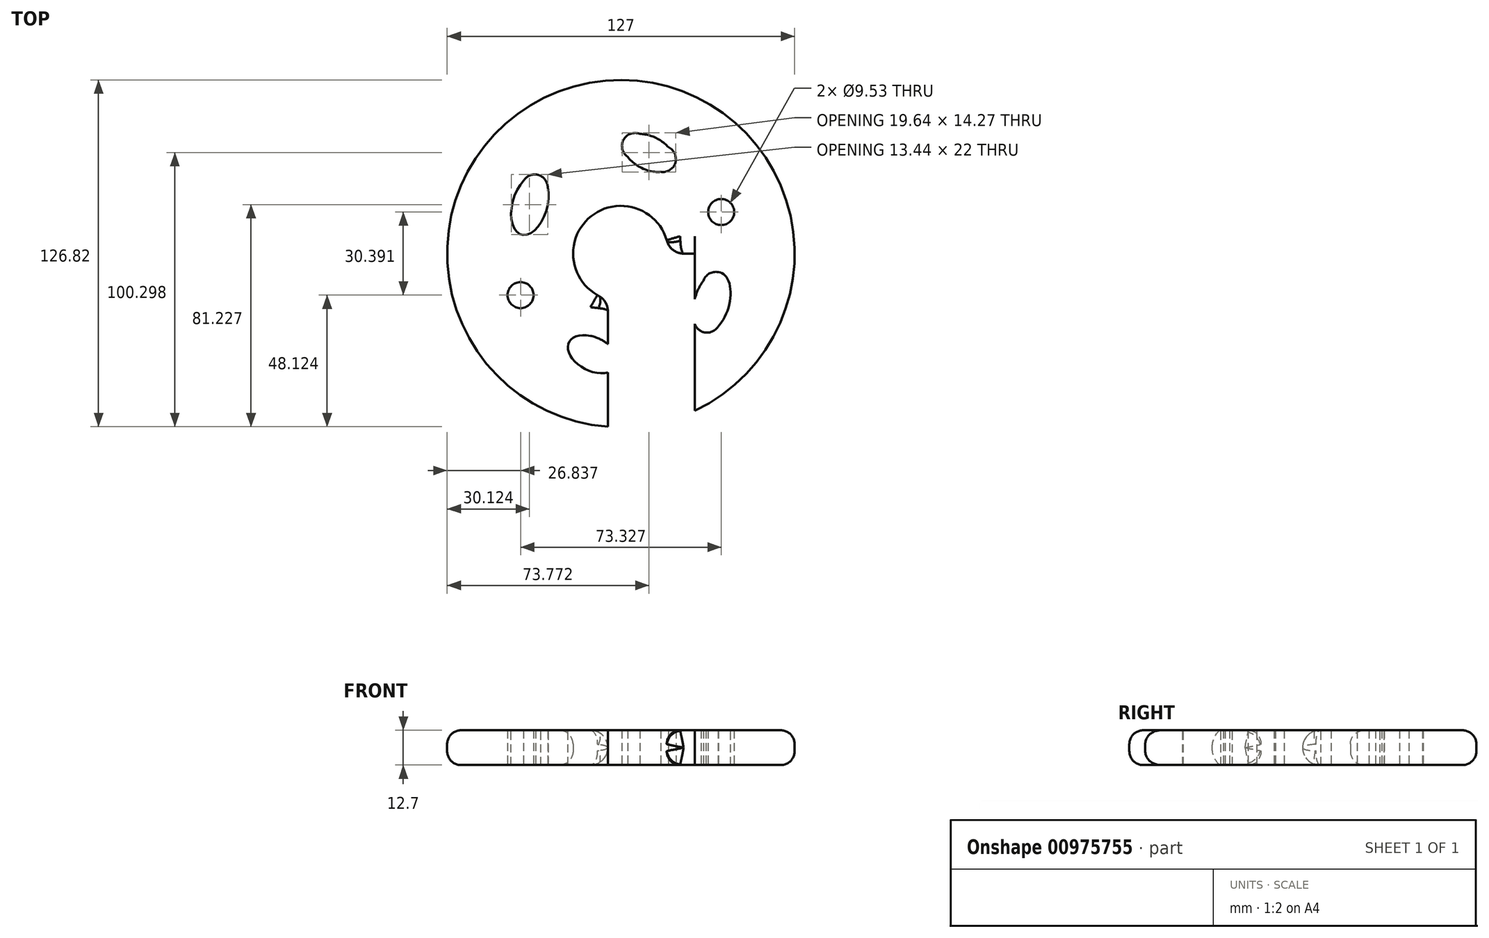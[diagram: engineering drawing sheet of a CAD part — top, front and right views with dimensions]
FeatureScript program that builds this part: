
annotation { "Feature Type Name" : "Feature", "Feature Type Description" : "" }
export const myFeature = defineFeature(function(context is Context, id is Id, definition is map)
    precondition{}
    {
        {
            var Q0;
            Q0=qCreatedBy(makeId("Top.planeOp"),FACE);
            var sketch = newSketch(context, id + "F0", { "sketchPlane" : qUnion([Q0])});
            skCircle(sketch, "E0", {"center": v(0, 0) * mm, "radius": 63.5 * mm});
            skCircle(sketch, "E1", {"center": v(0, 0) * mm, "radius": 17.46 * mm});
            skCircle(sketch, "E2", {"center": v(31.5, -24.15) * mm, "radius": 4.76 * mm});
            skCircle(sketch, "E3.1.0", {"center": v(36.66, 15.2) * mm, "radius": 4.76 * mm});
            skCircle(sketch, "E3.2.0", {"center": v(5.17, 39.35) * mm, "radius": 4.76 * mm});
            skCircle(sketch, "E3.3.0", {"center": v(-31.5, 24.15) * mm, "radius": 4.76 * mm});
            skCircle(sketch, "E3.4.0", {"center": v(-36.66, -15.2) * mm, "radius": 4.76 * mm});
            skCircle(sketch, "E3.5.0", {"center": v(-5.17, -39.35) * mm, "radius": 4.76 * mm});
            skCircle(sketch, "E4", {"center": v(34.67, -11.45) * mm, "radius": 4.76 * mm});
            skCircle(sketch, "E5", {"center": v(-13.19, -29.5) * mm, "radius": 4.76 * mm});
            skCircle(sketch, "E6", {"center": v(-40.13, 9.65) * mm, "radius": 4.76 * mm});
            skCircle(sketch, "E7", {"center": v(15.34, 34.59) * mm, "radius": 4.76 * mm});
            skEllipse(sketch, "E8", {"center": v(33.25, -17.84) * mm, "majorRadius": 11.35 * mm, "minorRadius": 6.37 * mm, "majorAxis": v(0.27, 0.96)});
            skEllipse(sketch, "E9.1.0", {"center": v(-33.25, 17.84) * mm, "majorRadius": 11.35 * mm, "minorRadius": 6.37 * mm, "majorAxis": v(-0.27, -0.96)});
            skEllipse(sketch, "E10", {"center": v(10.2, 36.8) * mm, "majorRadius": 9.78 * mm, "minorRadius": 6.1 * mm, "majorAxis": v(-0.9, 0.44)});
            skEllipse(sketch, "E11.1.0", {"center": v(-10.2, -36.8) * mm, "majorRadius": 9.78 * mm, "minorRadius": 6.1 * mm, "majorAxis": v(0.9, -0.44)});
            skSolve(sketch);
        }
        {
            var Q0;
            Q0=makeQuery(id+"F0.imprint","IMPRINT",FACE,{"disambiguationData":[TD([[makeQuery(id+"F0.imprint","IMPRINT",EDGE,{"derivedFrom":sQuery(id+"F0.wireOp",EDGE,"E0")}),1.0]])]});
            var Q1;
            {var subQ0=sQuery(id+"F0.wireOp",EDGE,"E11.1.0");var subQ1=sQuery(id+"F0.wireOp",EDGE,"E5");var subQ2=makeQuery(id+"F0.imprint","INTERSECT",VERTEX,{"disambiguationData":[OD(0.0)],"derivedFrom":[subQ1,subQ0]});Q1=makeQuery(id+"F0.imprint","IMPRINT",FACE,{"disambiguationData":[TD([[makeQuery(id+"F0.imprint","IMPRINT",EDGE,{"disambiguationData":[TD([[subQ2,-1.0]])],"derivedFrom":subQ1}),1.0]])]});}
            var Q2;
            {var subQ0=sQuery(id+"F0.wireOp",EDGE,"E11.1.0");var subQ1=sQuery(id+"F0.wireOp",EDGE,"E3.5.0");var subQ2=makeQuery(id+"F0.imprint","INTERSECT",VERTEX,{"disambiguationData":[OD(0.0)],"derivedFrom":[subQ1,subQ0]});Q2=makeQuery(id+"F0.imprint","IMPRINT",FACE,{"disambiguationData":[TD([[makeQuery(id+"F0.imprint","IMPRINT",EDGE,{"disambiguationData":[TD([[subQ2,1.0]])],"derivedFrom":subQ1}),1.0]])]});}
            var Q3;
            {var subQ0=sQuery(id+"F0.wireOp",EDGE,"E9.1.0");var subQ1=sQuery(id+"F0.wireOp",EDGE,"E6");var subQ2=makeQuery(id+"F0.imprint","INTERSECT",VERTEX,{"disambiguationData":[OD(0.0)],"derivedFrom":[subQ1,subQ0]});Q3=makeQuery(id+"F0.imprint","IMPRINT",FACE,{"disambiguationData":[TD([[makeQuery(id+"F0.imprint","IMPRINT",EDGE,{"disambiguationData":[TD([[subQ2,1.0]])],"derivedFrom":subQ1}),1.0]])]});}
            extrude(context, id + "F1", {"entities" : qUnion([Q0, Q1, Q2, Q3]), "depth" : 12.7 * mm, "offsetDistance" : 25.4 * mm});
        }
        {
            var Q0;
            Q0=makeQuery(id+"F1.opExtrude","CAP_EDGE",EDGE,{"disambiguationData":[OSD([sQuery(id+"F0.wireOp",EDGE,"E0")])],"isStart":false});
            var Q1;
            Q1=makeQuery(id+"F1.opExtrude","CAP_EDGE",EDGE,{"disambiguationData":[OSD([sQuery(id+"F0.wireOp",EDGE,"E0")])],"isStart":true});
            var Q2;
            Q2=makeQuery(id+"F1.opExtrude","CAP_EDGE",EDGE,{"disambiguationData":[OSD([sQuery(id+"F0.wireOp",EDGE,"E1")])],"isStart":true});
            var Q3;
            Q3=makeQuery(id+"F1.opExtrude","CAP_EDGE",EDGE,{"disambiguationData":[OSD([sQuery(id+"F0.wireOp",EDGE,"E1")])],"isStart":false});
            fillet(context, id + "F2", {"entities" : qUnion([Q0, Q1, Q2, Q3]), "radius" : 5.08 * mm, "tangentPropagation" : true, "allowEdgeOverflow" : false});
        }
        {
            var Q0;
            Q0=makeQuery(id+"F1.opExtrude","CAP_FACE",FACE,{"disambiguationData":[OSD([sQuery(id+"F0.wireOp",EDGE,"E0"),sQuery(id+"F0.wireOp",EDGE,"E1"),sQuery(id+"F0.wireOp",EDGE,"E2"),sQuery(id+"F0.wireOp",EDGE,"E3.1.0"),sQuery(id+"F0.wireOp",EDGE,"E3.2.0"),sQuery(id+"F0.wireOp",EDGE,"E3.3.0"),sQuery(id+"F0.wireOp",EDGE,"E3.4.0"),sQuery(id+"F0.wireOp",EDGE,"E4"),sQuery(id+"F0.wireOp",EDGE,"E7"),sQuery(id+"F0.wireOp",EDGE,"E8"),sQuery(id+"F0.wireOp",EDGE,"E9.1.0"),sQuery(id+"F0.wireOp",EDGE,"E10"),sQuery(id+"F0.wireOp",EDGE,"E11.1.0")])],"isStart":false});
            var sketch = newSketch(context, id + "F3", { "sketchPlane" : qUnion([Q0])});
            skLineSegment(sketch, "E12.bottom", {"start": v(-4.76, 0) * mm, "end": v(26.99, 0) * mm});
            skLineSegment(sketch, "E12.top", {"start": v(-4.76, -112.46) * mm, "end": v(26.99, -112.46) * mm});
            skLineSegment(sketch, "E12.left", {"start": v(-4.76, 0) * mm, "end": v(-4.76, -112.46) * mm});
            skLineSegment(sketch, "E12.right", {"start": v(26.99, 0) * mm, "end": v(26.99, -112.46) * mm});
            skSolve(sketch);
        }
        {
            var Q0;
            {var subQ0=sQuery(id+"F3.wireOp",EDGE,"E12.top");Q0=makeQuery(id+"F3.imprint","IMPRINT",FACE,{"disambiguationData":[TD([[makeQuery(id+"F3.imprint","IMPRINT",EDGE,{"derivedFrom":subQ0}),1.0]])]});}
            var Q1;
            {var subQ9=sQuery(id+"F3.wireOp",EDGE,"E12.left");var subQ10=sQuery(id+"F0.wireOp",EDGE,"E11.1.0");var subQ16=makeQuery(id+"F1.opExtrude","CAP_EDGE",EDGE,{"disambiguationData":[OSD([subQ10])],"isStart":false});var subQ17=makeQuery(id+"F3.imprint","INTERSECT",VERTEX,{"disambiguationData":[OD(0.0)],"derivedFrom":[subQ16,subQ9]});Q1=makeQuery(id+"F3.imprint","IMPRINT",FACE,{"disambiguationData":[TD([[makeQuery(id+"F3.imprint","IMPRINT",EDGE,{"disambiguationData":[TD([[subQ17,1.0]])],"derivedFrom":subQ16}),-1.0]])]});}
            var Q2;
            {var subQ0=sQuery(id+"F3.wireOp",EDGE,"E12.left");var subQ1=sQuery(id+"F3.wireOp",EDGE,"E12.bottom");var subQ2=makeQuery(id+"F3.imprint","INTERSECT",VERTEX,{"derivedFrom":[subQ1,subQ0]});Q2=makeQuery(id+"F3.imprint","IMPRINT",FACE,{"disambiguationData":[TD([[makeQuery(id+"F3.imprint","IMPRINT",EDGE,{"disambiguationData":[TD([[subQ2,-1.0]])],"derivedFrom":subQ1}),-1.0]])]});}
            extrude(context, id + "F4", {"entities" : qUnion([Q0, Q1, Q2]), "operationType" : NewBodyOperationType.REMOVE, "oppositeDirection" : true, "depth" : 25.4 * mm, "offsetDistance" : 25.4 * mm});
        }
        {
            var Q0;
            {var subQ0=sQuery(id+"F0.wireOp",EDGE,"E1");Q0=makeQuery(id+"F4.boolean.opBoolean","INTERSECT",EDGE,{"derivedFrom":[makeQuery(id+"F2.opFillet","BLEND_FACE",FACE,{"disambiguationData":[OSD([subQ0]),TDD([makeQuery(id+"F1.opExtrude","CAP_EDGE",EDGE,{"disambiguationData":[OSD([subQ0])],"isStart":true})])]}),makeQuery(id+"F4.opExtrude","SWEPT_FACE",FACE,{"disambiguationData":[OSD([sQuery(id+"F3.wireOp",EDGE,"E12.bottom")])]})]});}
            var Q1;
            {var subQ0=sQuery(id+"F3.wireOp",EDGE,"E12.left");var subQ1=sQuery(id+"F0.wireOp",EDGE,"E11.1.0");var subQ2=sQuery(id+"F0.wireOp",EDGE,"E1");Q1=makeQuery(id+"F4.boolean.opBoolean","INTERSECT",EDGE,{"derivedFrom":[makeQuery(id+"F1.opExtrude","SWEPT_FACE",FACE,{"disambiguationData":[OSD([subQ2])]}),makeQuery(id+"F4.opExtrude","SWEPT_FACE",FACE,{"disambiguationData":[OSD([subQ0]),TDD([makeQuery(id+"F3.imprint","IMPRINT",EDGE,{"disambiguationData":[TD([[makeQuery(id+"F3.imprint","INTERSECT",VERTEX,{"derivedFrom":[sQuery(id+"F3.wireOp",EDGE,"E12.bottom"),subQ0]}),-1.0]])],"derivedFrom":subQ0}),makeQuery(id+"F3.imprint","IMPRINT",EDGE,{"disambiguationData":[TD([[makeQuery(id+"F3.imprint","INTERSECT",VERTEX,{"disambiguationData":[OD(0.0)],"derivedFrom":[makeQuery(id+"F1.opExtrude","CAP_EDGE",EDGE,{"disambiguationData":[OSD([subQ1])],"isStart":false}),subQ0]}),1.0]])],"derivedFrom":subQ0})])]})]});}
            fillet(context, id + "F5", {"entities" : qUnion([Q0, Q1]), "radius" : 6.35 * mm, "tangentPropagation" : true, "allowEdgeOverflow" : false});
        }
    });
